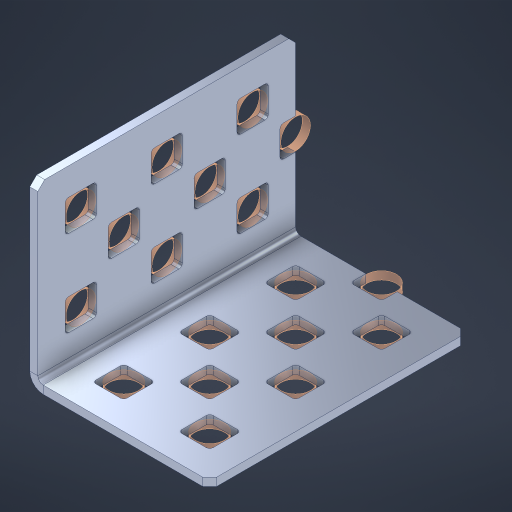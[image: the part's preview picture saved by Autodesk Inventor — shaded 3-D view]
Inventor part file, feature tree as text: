
AUTODESK INVENTOR PART (.ipt)
format: ipt  version: 2023 (Build 270158000, 158)  size: 542,208 bytes
history: native  units: in
note: dims shown in document units (in); Inventor stores cm internally (conversion verified against a paired STEP export)
features: other x24, extrude x16, sheet_metal_op x8, sketch x7, pattern_linear x2, mirror x1, chamfer x1
ambient origin geometry x8: Origin, YZ Plane, XZ Plane, XY Plane, X Axis, Y Axis, Z Axis, Center Point
bodies: Solid1 (feature_tree), Body (feature_tree)
feature tree (59):
  sheet_metal_op  "Flanges"
  sheet_metal_op  "Body Pattern"
  pattern_linear  "Center Pattern"  Spacing1=1.0in  [1 undecoded]
  other  "Arc Length"
  pattern_linear  "Notch Pattern"  Spacing1=0.1875in  [1 undecoded]
  other  "Diagonal Plane"
  mirror  "Everything Mirrored"
  chamfer  "End Chamfer"
  sketch  "Sketch1"  dims[d0=1.0in]
  other  "Plate1"
  sketch  "Sketch2"  dims[d1=1.5in]
  other  "Plate2"
  sheet_metal_op  "Bend1"
  sheet_metal_op  "Corner1"
  sketch  "Sketch8"  dims[d2=0.0469in]
  sketch  "Sketch9"  dims[d3=0.0469in]
  other  "Srf91"
  sheet_metal_op  "Body Pattern Sketch"
  other  "Srf92"
  sketch  "Sketch13"  dims[d4=0.0234in]
  sketch  "Sketch15"  dims[d5=0.0938in]
  sketch  "Sketch16"  dims[d6=0.0469in d7=1.0in d8=90.0deg d9=0.0312in d10=0.1875in d11=0.0469in d12=0.0469in d49=0.182in d50=0.02in d52=0.25in d53=0.0469in d54=0.0in d55=0.172in d56=1.0in d57=0.0in d60=1.1811in d62=0.5in d63=0.7874in d65=0.5in d85=0.1473in d86=0.1659in d89=0.0469in d90=0.0in d91=0.04in d92=0.0491in d95=2.5in d96=0.04in d97=0.25in d98=45.0deg d99=0.25in d106=0.182in d107=0.02in d108=0.5in d110=0.0469in d111=0.0in d112=0.172in d113=0.5in d114=0.0in d117=0.5in d123=0.25in d125=0.25in d126=0.0491in d127=0.1227in d128=0.08in d129=0.04in d130=2.5in]
  other  "Srf786"
  other  "Srf856"
  other  "Srf857"
  other  "Srf858"
  other  "Srf859"
  other  "Srf889"
  other  "Srf890"
  other  "Srf1275"
  other  "Srf1276"
  other  "Srf1278"
  other  "Srf1279"
  other  "Srf1280"
  other  "Srf1281"
  other  "Srf1277"
  other  "Srf1285"
  other  "Srf1286"
  sheet_metal_op  "Body Stamp"
  sheet_metal_op  "Body Circle"
  other  "Center Stamp"
  other  "Center Circle"
  sheet_metal_op  "Notch"
  extrude  "ExtrusionSrf92"  Depth=0.0469in
  extrude  "ExtrusionSrf856"  Depth=0.0469in
  extrude  "ExtrusionSrf857"  Depth=0.182in
  extrude  "ExtrusionSrf858"  Depth=0.02in
  extrude  "ExtrusionSrf859"  Depth=0.25in
  extrude  "ExtrusionSrf889"  Depth=0.0469in
  extrude  "ExtrusionSrf890"  TaperAngle=0.0deg  [1 undecoded]
  extrude  "ExtrusionSrf1275"  Depth=0.25in
  extrude  "ExtrusionSrf1276"  Depth=1.0in TaperAngle=0.0deg
  extrude  "ExtrusionSrf1277"  Depth=0.25in
  extrude  "ExtrusionSrf1278"  Depth=0.5in
  extrude  "ExtrusionSrf1279"  Depth=0.25in
  extrude  "ExtrusionSrf1280"  Depth=0.25in
  extrude  "ExtrusionSrf1345"  Depth=0.0469in
  extrude  "ExtrusionSrf1346"  Depth=0.25in TaperAngle=0.0deg
  extrude  "ExtrusionSrf1347"  Depth=0.25in
note: 3 required parameter values undecoded (feature->parameter linkage not recoverable at this tier; creation-order binding heuristic only, values carry confidence <= 0.55)
